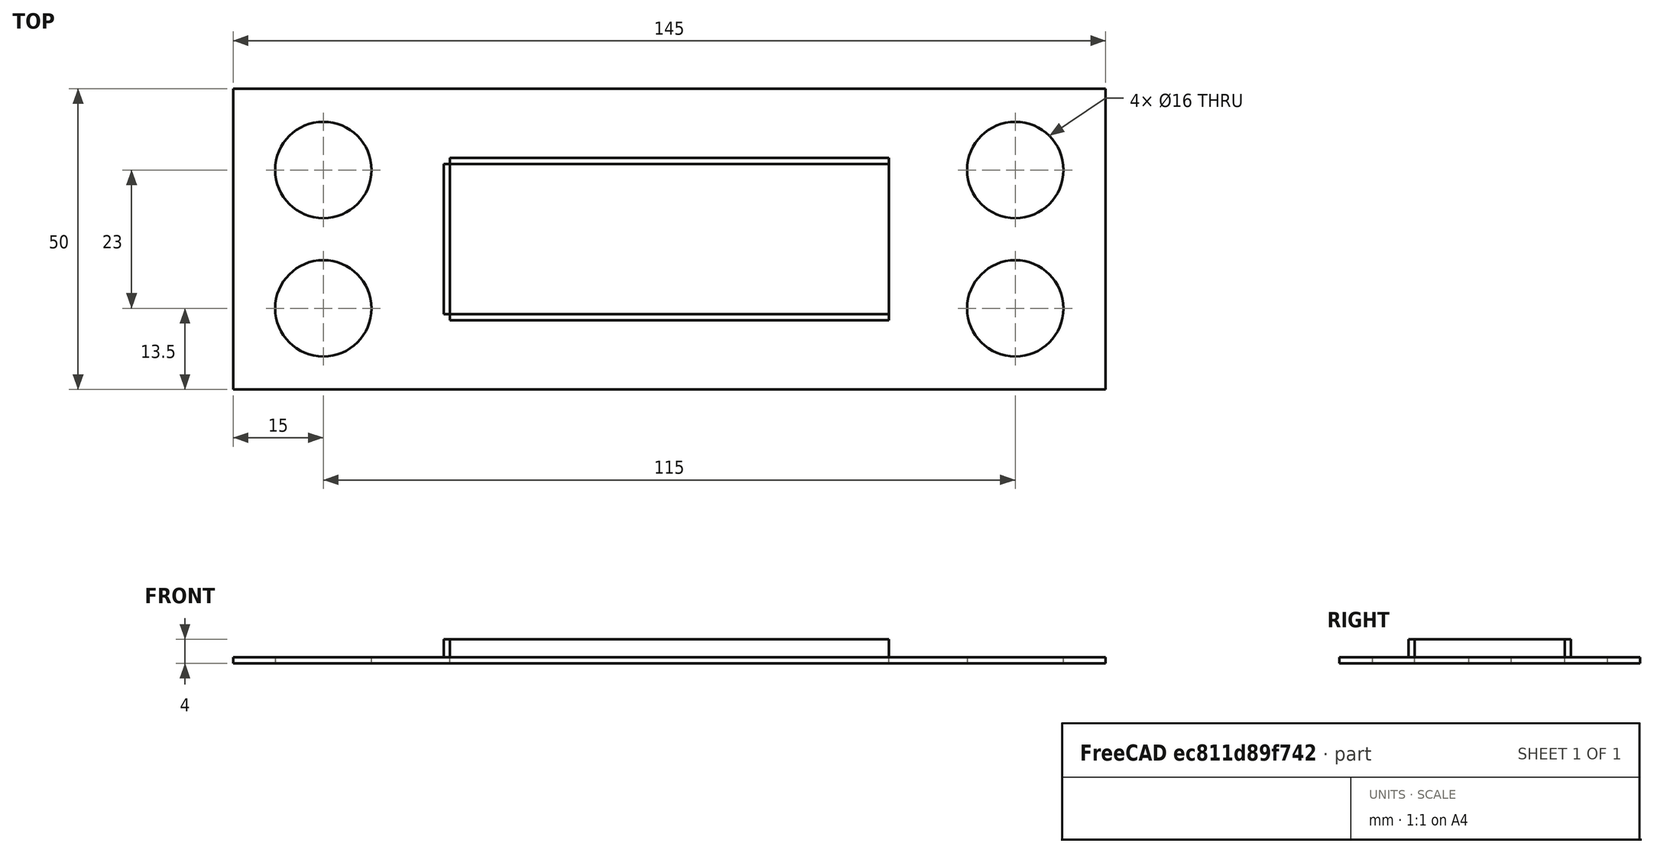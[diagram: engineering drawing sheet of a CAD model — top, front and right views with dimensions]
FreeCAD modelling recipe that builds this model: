
FCSTD DOCUMENT  (FreeCAD 0.21R33668 +26 (Git))
Label: Stopuhr-V01
License: All rights reserved
LicenseURL: https://en.wikipedia.org/wiki/All_rights_reserved
objects: Sketcher::SketchObject×2, PartDesign::Pad×2, PartDesign::Body×1
note: 7 computed .brp shape members not serialized (recipe doc carries the construction recipe); baked Part::Feature solids carry a one-line shape summary decoded from their .brp

FEATURE [Sketcher::SketchObject] Sketch
  FullyConstrained = true
  MapMode = 5
  Support = -> [XY_Plane]
  sketch-geometry (23):
    g0: LineSegment StartX=0 StartY=0 StartZ=0 EndX=145 EndY=0 EndZ=0
    g1: LineSegment StartX=145 StartY=0 StartZ=0 EndX=145 EndY=50 EndZ=0
    g2: LineSegment StartX=145 StartY=50 StartZ=0 EndX=0 EndY=50 EndZ=0
    g3: LineSegment StartX=0 StartY=50 StartZ=0 EndX=0 EndY=0 EndZ=0
    g4: LineSegment StartX=36 StartY=12.5 StartZ=0 EndX=109 EndY=12.5 EndZ=0
    g5: LineSegment StartX=109 StartY=12.5 StartZ=0 EndX=109 EndY=37.5 EndZ=0
    g6: LineSegment StartX=109 StartY=37.5 StartZ=0 EndX=36 EndY=37.5 EndZ=0
    g7: LineSegment StartX=36 StartY=37.5 StartZ=0 EndX=36 EndY=12.5 EndZ=0
    g8: LineSegment StartX=109 StartY=37.5 StartZ=0 EndX=145 EndY=37.5 EndZ=0
    g9: LineSegment StartX=36 StartY=37.5 StartZ=0 EndX=36 EndY=50 EndZ=0
    g10: LineSegment StartX=36 StartY=12.5 StartZ=0 EndX=36 EndY=0 EndZ=0
    g11: Circle CenterX=15 CenterY=13.5 CenterZ=0 NormalX=0 NormalY=0 NormalZ=1 AngleXU=0 Radius=8
    g12: Circle CenterX=15 CenterY=36.5 CenterZ=0 NormalX=0 NormalY=0 NormalZ=1 AngleXU=0 Radius=8
    g13: Circle CenterX=130 CenterY=13.5 CenterZ=0 NormalX=0 NormalY=0 NormalZ=1 AngleXU=0 Radius=8
    g14: LineSegment StartX=15 StartY=36.5 StartZ=0 EndX=15 EndY=13.5 EndZ=0
    g15: LineSegment StartX=130 StartY=36.5 StartZ=0 EndX=130 EndY=13.5 EndZ=0
    g16: Circle CenterX=130 CenterY=36.5 CenterZ=0 NormalX=0 NormalY=0 NormalZ=1 AngleXU=0 Radius=8
    g17: LineSegment StartX=15 StartY=36.5 StartZ=0 EndX=15 EndY=50 EndZ=0
    g18: LineSegment StartX=15 StartY=13.5 StartZ=0 EndX=15 EndY=0 EndZ=0
    g19: LineSegment StartX=15 StartY=13.5 StartZ=0 EndX=130 EndY=13.5 EndZ=0
    g20: LineSegment StartX=15 StartY=36.5 StartZ=0 EndX=0 EndY=36.5 EndZ=0
    g21: LineSegment StartX=130 StartY=36.5 StartZ=0 EndX=145 EndY=36.5 EndZ=0
    g22: LineSegment StartX=36 StartY=37.5 StartZ=0 EndX=0 EndY=37.5 EndZ=0
  constraints (65):
    c: Coincident(g0,g1)
    c: Coincident(g1,g2)
    c: Coincident(g2,g3)
    c: Coincident(g3,g0)
    c: Horizontal(g0)
    c: Horizontal(g2)
    c: Vertical(g1)
    c: Vertical(g3)
    c: Coincident(g0,g-1)
    c: DistanceY(g1,g1) = 50
    c: DistanceX(g2,g2) = 145
    c: Coincident(g4,g5)
    c: Coincident(g5,g6)
    c: Coincident(g6,g7)
    c: Coincident(g7,g4)
    c: Horizontal(g4)
    c: Horizontal(g6)
    c: Vertical(g5)
    c: Vertical(g7)
    c: DistanceY(g5,g5) = 25
    c: DistanceX(g6,g6) = 73
    c: Coincident(g8,g5)
    c: PointOnObject(g8,g1)
    c: Horizontal(g8)
    c: Coincident(g9,g6)
    c: PointOnObject(g9,g2)
    c: Vertical(g9)
    c: Coincident(g10,g4)
    c: PointOnObject(g10,g0)
    c: Vertical(g10)
    c: Equal(g9,g10)
    c: Radius(g11) = 8
    c: Equal(g12,g11)
    c: Coincident(g14,g12)
    c: Coincident(g14,g11)
    c: Coincident(g15,g13)
    c: Vertical(g15)
    c: Vertical(g14)
    c: Equal(g14,g15)
    c: Equal(g16,g11)
    c: Coincident(g16,g15)
    c: DistanceY(g14,g14) = 23
    c: Coincident(g17,g12)
    c: PointOnObject(g17,g2)
    c: Vertical(g17)
    c: Coincident(g18,g11)
    c: PointOnObject(g18,g0)
    c: Vertical(g18)
    c: Equal(g18,g17)
    c: Coincident(g19,g11)
    c: Coincident(g19,g13)
    c: Horizontal(g19)
    c: Equal(g13,g11)
    c: Coincident(g20,g12)
    c: PointOnObject(g20,g3)
    c: Horizontal(g20)
    c: Coincident(g21,g16)
    c: PointOnObject(g21,g1)
    c: Horizontal(g21)
    c: Equal(g21,g20)
    c: DistanceX(g20,g20) = 15
    c: Coincident(g22,g6)
    c: PointOnObject(g22,g3)
    c: Horizontal(g22)
    c: Equal(g8,g22)
FEATURE [PartDesign::Pad] Pad
  Direction = (0,0,1)
  Length = 1
  Length2 = 10
  Profile = -> Sketch
  ReferenceAxis = -> Sketch [N_Axis]
  Type = 0
FEATURE [Sketcher::SketchObject] Sketch001
  ExternalGeometry = -> [Pad]
  FullyConstrained = true
  MapMode = 5
  Placement = pos=(0,0,1) rot=(0,0,1;0rad)
  Support = -> [Pad]
  sketch-geometry (12):
    g0: LineSegment StartX=36 StartY=12.5 StartZ=0 EndX=109 EndY=12.5 EndZ=0
    g1: LineSegment StartX=109 StartY=12.5 StartZ=0 EndX=109 EndY=11.5 EndZ=0
    g2: LineSegment StartX=109 StartY=11.5 StartZ=0 EndX=36 EndY=11.5 EndZ=0
    g3: LineSegment StartX=36 StartY=11.5 StartZ=0 EndX=36 EndY=12.5 EndZ=0
    g4: LineSegment StartX=36 StartY=37.5 StartZ=0 EndX=109 EndY=37.5 EndZ=0
    g5: LineSegment StartX=109 StartY=37.5 StartZ=0 EndX=109 EndY=38.5 EndZ=0
    g6: LineSegment StartX=109 StartY=38.5 StartZ=0 EndX=36 EndY=38.5 EndZ=0
    g7: LineSegment StartX=36 StartY=38.5 StartZ=0 EndX=36 EndY=37.5 EndZ=0
    g8: LineSegment StartX=36 StartY=12.5 StartZ=0 EndX=35 EndY=12.5 EndZ=0
    g9: LineSegment StartX=35 StartY=12.5 StartZ=0 EndX=35 EndY=37.5 EndZ=0
    g10: LineSegment StartX=35 StartY=37.5 StartZ=0 EndX=36 EndY=37.5 EndZ=0
    g11: LineSegment StartX=36 StartY=37.5 StartZ=0 EndX=36 EndY=12.5 EndZ=0
  constraints (30):
    c: Coincident(g0,g1)
    c: Coincident(g1,g2)
    c: Coincident(g2,g3)
    c: Coincident(g3,g0)
    c: Horizontal(g2)
    c: Vertical(g1)
    c: Vertical(g3)
    c: Coincident(g0,g-3)
    c: Coincident(g0,g-4)
    c: DistanceY(g3,g3) = 1
    c: Coincident(g4,g5)
    c: Coincident(g5,g6)
    c: Coincident(g6,g7)
    c: Coincident(g7,g4)
    c: Horizontal(g6)
    c: Vertical(g5)
    c: Vertical(g7)
    c: Coincident(g4,g-3)
    c: Coincident(g-4,g4)
    c: DistanceY(g7,g7) = 1
    c: Coincident(g8,g9)
    c: Coincident(g9,g10)
    c: Coincident(g10,g11)
    c: Coincident(g11,g8)
    c: Horizontal(g8)
    c: Horizontal(g10)
    c: Vertical(g9)
    c: Coincident(g8,g0)
    c: Coincident(g4,g10)
    c: DistanceX(g10,g10) = 1
FEATURE [PartDesign::Pad] Pad001
  BaseFeature = -> Pad
  Direction = (0,0,1)
  Length = 3
  Length2 = 10
  Profile = -> Sketch001
  ReferenceAxis = -> Sketch001 [N_Axis]
  Type = 0
FEATURE [PartDesign::Body] Body  label="Körper"
  Group = -> [Sketch,Pad,Sketch001,Pad001]
  Origin = -> Origin
  Tip = -> Pad001
